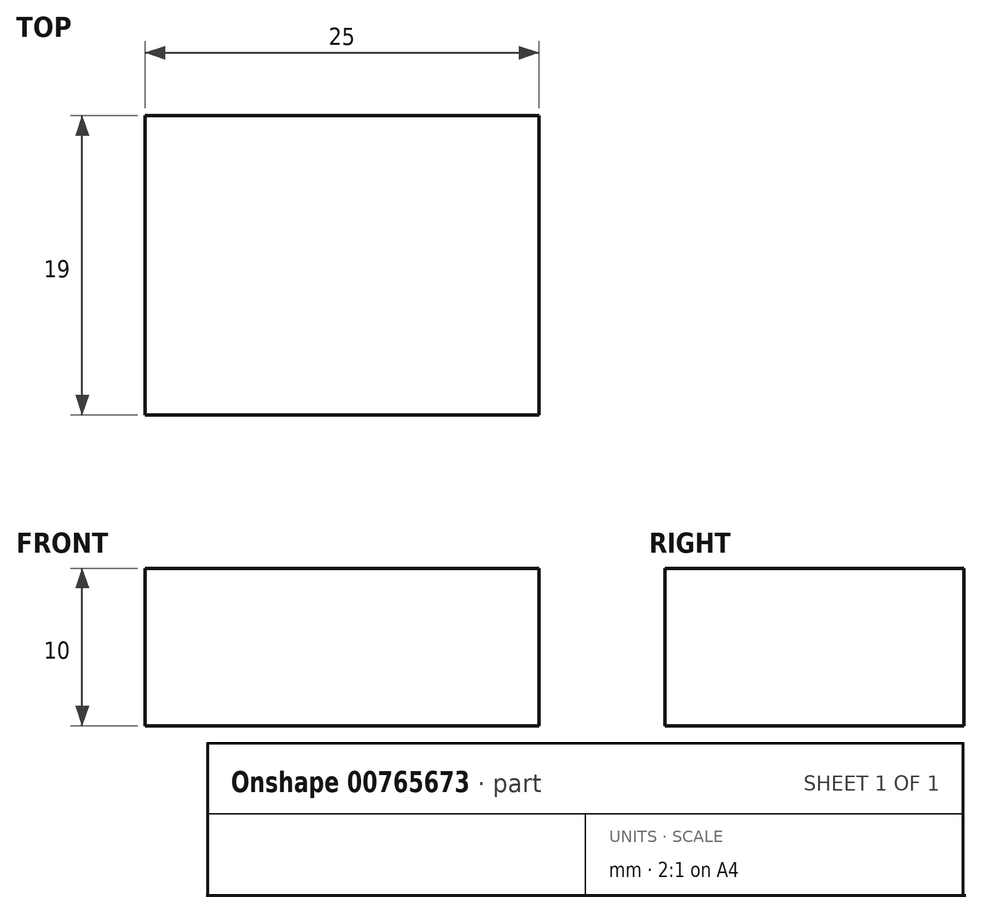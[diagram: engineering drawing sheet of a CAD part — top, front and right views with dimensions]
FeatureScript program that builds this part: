
annotation { "Feature Type Name" : "Feature", "Feature Type Description" : "" }
export const myFeature = defineFeature(function(context is Context, id is Id, definition is map)
    precondition{}
    {
        {
            var Q0;
            Q0=qCreatedBy(makeId("Top.planeOp"),FACE);
            var sketch = newSketch(context, id + "F0", { "sketchPlane" : qUnion([Q0])});
            skLineSegment(sketch, "E0.bottom", {"start": v(-9.06, -0.67) * mm, "end": v(15.94, -0.67) * mm});
            skLineSegment(sketch, "E0.top", {"start": v(-9.06, -19.67) * mm, "end": v(15.94, -19.67) * mm});
            skLineSegment(sketch, "E0.left", {"start": v(-9.06, -0.67) * mm, "end": v(-9.06, -19.67) * mm});
            skLineSegment(sketch, "E0.right", {"start": v(15.94, -0.67) * mm, "end": v(15.94, -19.67) * mm});
            skSolve(sketch);
        }
        {
            var Q0;
            Q0 = qSketchRegion(id + "F0", true);
            extrude(context, id + "F1", {"entities" : qUnion([Q0]), "depth" : 10 * mm, "offsetDistance" : 25.4 * mm});
        }
    });
